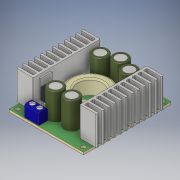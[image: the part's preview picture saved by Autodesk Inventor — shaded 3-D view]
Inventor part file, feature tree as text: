
AUTODESK INVENTOR PART (.ipt)
format: ipt  version: 2019 (Build 230136000, 136)  size: 695,808 bytes
history: native  units: mm
features: sketch x11, extrude x10, projected_geometry x5, fillet x3, other x1, hole x1, mirror x1, chamfer x1
ambient origin geometry x8: Origin, YZ Plane, XZ Plane, XY Plane, X Axis, Y Axis, Z Axis, Center Point
bodies: Body1 (feature_tree)
feature tree (33):
  other  "Твердое тело1"
  extrude  "Выдавливание1"  Depth=60.0mm
  hole  "Отверстие1"  [1 undecoded]
  extrude  "Выдавливание2"  Depth=1.6mm TaperAngle=0.0deg
  extrude  "Выдавливание3"  Depth=3.0mm
  fillet  "Сопряжение1"  Radius=3.0mm
  extrude  "Выдавливание4"  Depth=1.6mm
  extrude  "Выдавливание5"  Depth=46.0mm
  extrude  "Выдавливание6"  Depth=10.0mm
  extrude  "Выдавливание7"  Depth=2.0mm
  extrude  "Выдавливание8"  Depth=60.0mm
  fillet  "Сопряжение2"  Radius=20.0mm
  mirror  "Зеркальное отражение1"
  fillet  "Сопряжение3"  Radius=5.0mm
  extrude  "Выдавливание9"  Depth=17.0mm
  extrude  "Выдавливание10"  Depth=10.0mm TaperAngle=0.0deg
  chamfer  "Фаска1"  Distance=1.0mm
  sketch  "Эскиз1"
  sketch  "Эскиз2"
  sketch  "Эскиз3"
  sketch  "Эскиз4"
  sketch  "Эскиз5"
  sketch  "Эскиз6"
  projected_geometry  "Спроецированная петля1"
  projected_geometry  "Спроецированная петля2"
  projected_geometry  "Спроецированная петля3"
  projected_geometry  "Спроецированная петля4"
  projected_geometry  "Спроецированная петля5"
  sketch  "Эскиз8"
  sketch  "Эскиз9"
  sketch  "Эскиз10"
  sketch  "Эскиз11"
  sketch  "Эскиз12"
note: 1 required parameter value undecoded (feature->parameter linkage not recoverable at this tier; creation-order binding heuristic only, values carry confidence <= 0.55)
